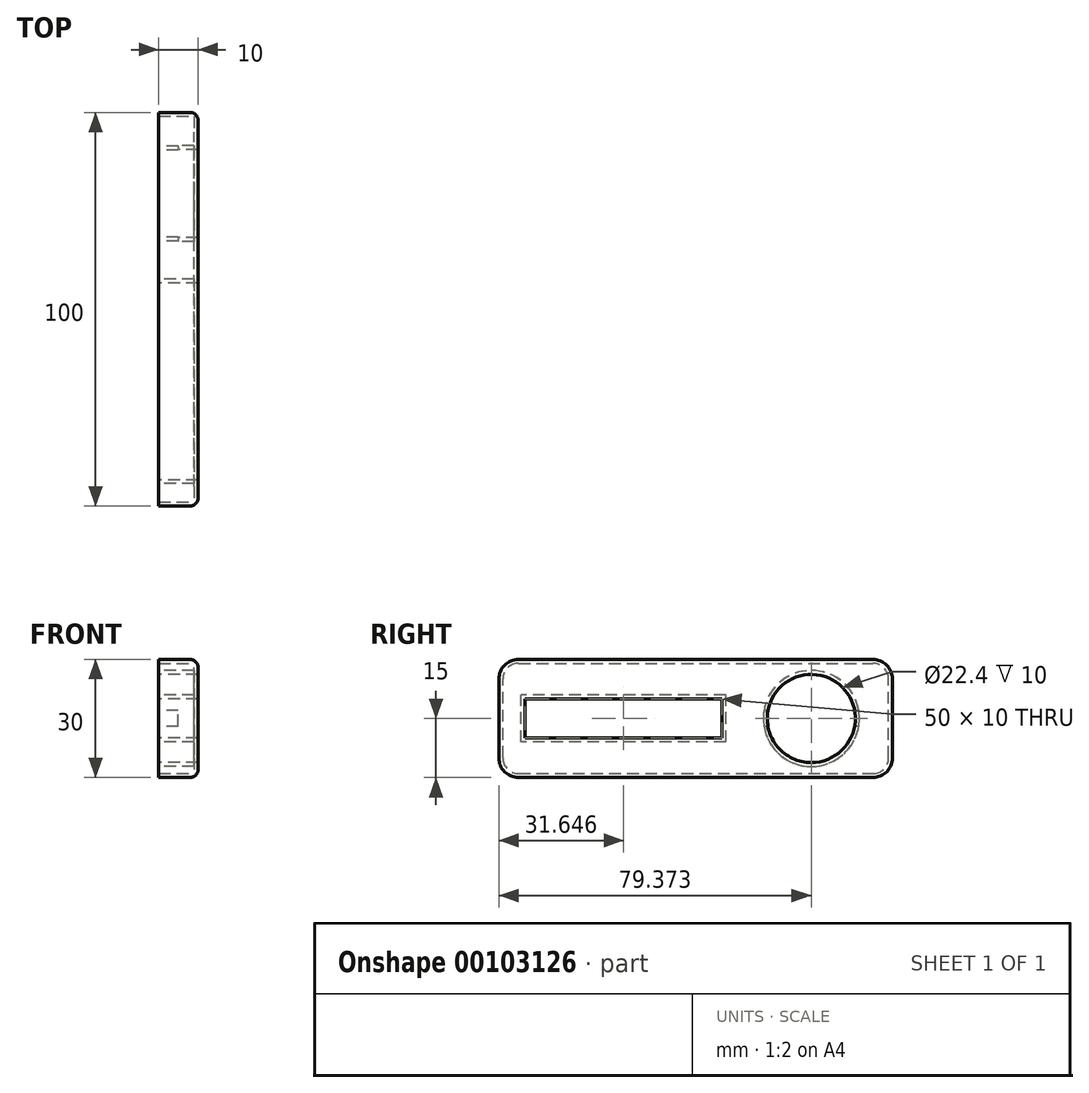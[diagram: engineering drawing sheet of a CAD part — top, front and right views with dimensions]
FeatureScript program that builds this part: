
annotation { "Feature Type Name" : "Feature", "Feature Type Description" : "" }
export const myFeature = defineFeature(function(context is Context, id is Id, definition is map)
    precondition{}
    {
        {
            var Q0;
            Q0=qCreatedBy(makeId("Right.planeOp"),FACE);
            var sketch = newSketch(context, id + "F0", { "sketchPlane" : qUnion([Q0])});
            skLineSegment(sketch, "E0.bottom", {"start": v(-45, -15) * mm, "end": v(45, -15) * mm});
            skLineSegment(sketch, "E0.top", {"start": v(-45, 15) * mm, "end": v(45, 15) * mm});
            skLineSegment(sketch, "E0.left", {"start": v(-50, -10) * mm, "end": v(-50, 10) * mm});
            skLineSegment(sketch, "E0.right", {"start": v(50, -10) * mm, "end": v(50, 10) * mm});
            skPoint(sketch, "E0.middle", {"position": v(0, 0) * mm});
            skPoint(sketch, "E1.visualSharp", {"position": v(50, 15) * mm});
            skArc(sketch, "E1.filletArc", {"start": v(50, 10) * mm, "mid": v(48.54, 13.54) * mm, "end": v(45, 15) * mm});
            skPoint(sketch, "E2.visualSharp", {"position": v(50, -15) * mm});
            skArc(sketch, "E2.filletArc", {"start": v(45, -15) * mm, "mid": v(48.54, -13.54) * mm, "end": v(50, -10) * mm});
            skPoint(sketch, "E3.visualSharp", {"position": v(-50, 15) * mm});
            skArc(sketch, "E3.filletArc", {"start": v(-45, 15) * mm, "mid": v(-48.54, 13.54) * mm, "end": v(-50, 10) * mm});
            skPoint(sketch, "E4.visualSharp", {"position": v(-50, -15) * mm});
            skArc(sketch, "E4.filletArc", {"start": v(-50, -10) * mm, "mid": v(-48.54, -13.54) * mm, "end": v(-45, -15) * mm});
            skLineSegment(sketch, "E5.bottom", {"start": v(6.65, -5) * mm, "end": v(-43.35, -5) * mm});
            skLineSegment(sketch, "E5.top", {"start": v(6.65, 5) * mm, "end": v(-43.35, 5) * mm});
            skLineSegment(sketch, "E5.left", {"start": v(6.65, -5) * mm, "end": v(6.65, 5) * mm});
            skLineSegment(sketch, "E5.right", {"start": v(-43.35, -5) * mm, "end": v(-43.35, 5) * mm});
            skPoint(sketch, "E5.middle", {"position": v(-18.35, 0) * mm});
            skCircle(sketch, "E6", {"center": v(29.37, 0) * mm, "radius": 11.2 * mm});
            skSolve(sketch);
        }
        {
            var Q0;
            Q0=makeQuery(id+"F0.imprint","IMPRINT",FACE,{"disambiguationData":[TD([[makeQuery(id+"F0.imprint","IMPRINT",EDGE,{"derivedFrom":sQuery(id+"F0.wireOp",EDGE,"E0.bottom")}),1.0]])]});
            extrude(context, id + "F1", {"entities" : qUnion([Q0]), "depth" : 10 * mm, "offsetDistance" : 25 * mm});
        }
        {
            var Q0;
            Q0=makeQuery(id+"F1.opExtrude","CAP_FACE",FACE,{"disambiguationData":[OSD([sQuery(id+"F0.wireOp",EDGE,"E0.bottom"),sQuery(id+"F0.wireOp",EDGE,"E0.top"),sQuery(id+"F0.wireOp",EDGE,"E0.left"),sQuery(id+"F0.wireOp",EDGE,"E0.right"),sQuery(id+"F0.wireOp",EDGE,"E1.filletArc"),sQuery(id+"F0.wireOp",EDGE,"E2.filletArc"),sQuery(id+"F0.wireOp",EDGE,"E3.filletArc"),sQuery(id+"F0.wireOp",EDGE,"E4.filletArc"),sQuery(id+"F0.wireOp",EDGE,"E5.bottom"),sQuery(id+"F0.wireOp",EDGE,"E5.top"),sQuery(id+"F0.wireOp",EDGE,"E5.left"),sQuery(id+"F0.wireOp",EDGE,"E5.right"),sQuery(id+"F0.wireOp",EDGE,"E6")])],"isStart":true});
            shell(context, id + "F2", {"entities" : qUnion([Q0]), "thickness" : 1 * mm});
        }
        {
            var Q0;
            Q0=makeQuery(id+"F1.opExtrude","CAP_EDGE",EDGE,{"disambiguationData":[OSD([sQuery(id+"F0.wireOp",EDGE,"E0.bottom")])],"isStart":false});
            fillet(context, id + "F3", {"entities" : qUnion([Q0]), "tangentPropagation" : true, "radius" : 2 * mm, "defaultsChanged" : false, "vertexSettings" : [], "allowEdgeOverflow" : false});
        }
        {
            var Q0;
            {var subQ0=sQuery(id+"F0.wireOp",EDGE,"E6");var subQ1=sQuery(id+"F0.wireOp",EDGE,"E5.right");var subQ2=sQuery(id+"F0.wireOp",EDGE,"E5.left");var subQ3=sQuery(id+"F0.wireOp",EDGE,"E5.top");var subQ4=sQuery(id+"F0.wireOp",EDGE,"E5.bottom");var subQ5=sQuery(id+"F0.wireOp",EDGE,"E4.filletArc");var subQ6=sQuery(id+"F0.wireOp",EDGE,"E3.filletArc");var subQ7=sQuery(id+"F0.wireOp",EDGE,"E2.filletArc");var subQ8=sQuery(id+"F0.wireOp",EDGE,"E1.filletArc");var subQ9=sQuery(id+"F0.wireOp",EDGE,"E0.right");var subQ10=sQuery(id+"F0.wireOp",EDGE,"E0.left");var subQ11=sQuery(id+"F0.wireOp",EDGE,"E0.top");var subQ12=sQuery(id+"F0.wireOp",EDGE,"E0.bottom");Q0=makeQuery(id+"F2.opShell","OFFSET_FACE",FACE,{"disambiguationData":[OSD([subQ12,subQ11,subQ10,subQ9,subQ8,subQ7,subQ6,subQ5,subQ4,subQ3,subQ2,subQ1,subQ0]),TDD([makeQuery(id+"F1.opExtrude","CAP_FACE",FACE,{"disambiguationData":[OSD([subQ12,subQ11,subQ10,subQ9,subQ8,subQ7,subQ6,subQ5,subQ4,subQ3,subQ2,subQ1,subQ0])],"isStart":true})]),OD(1.0)]});}
            var sketch = newSketch(context, id + "F4", { "sketchPlane" : qUnion([Q0])});
            skLineSegment(sketch, "E7.bottom", {"start": v(-43.37, 2) * mm, "end": v(-15.37, 2) * mm});
            skLineSegment(sketch, "E7.top", {"start": v(-43.37, -2) * mm, "end": v(-15.37, -2) * mm});
            skLineSegment(sketch, "E7.left", {"start": v(-43.37, 2) * mm, "end": v(-43.37, -2) * mm});
            skLineSegment(sketch, "E7.right", {"start": v(-15.37, 2) * mm, "end": v(-15.37, -2) * mm});
            skPoint(sketch, "E7.middle", {"position": v(-29.37, 0) * mm});
            skSolve(sketch);
        }
        {
            var Q0;
            {var subQ0=sQuery(id+"F4.wireOp",EDGE,"E7.bottom");var subQ1=makeQuery(id+"F1.opExtrude","CAP_EDGE",EDGE,{"disambiguationData":[OSD([sQuery(id+"F0.wireOp",EDGE,"E6")])],"isStart":true});var subQ2=makeQuery(id+"F4.imprint","INTERSECT",VERTEX,{"disambiguationData":[OD(0.0)],"derivedFrom":[subQ1,subQ0]});Q0=makeQuery(id+"F4.imprint","IMPRINT",FACE,{"disambiguationData":[TD([[makeQuery(id+"F4.imprint","IMPRINT",EDGE,{"disambiguationData":[TD([[subQ2,-1.0]])],"derivedFrom":subQ0}),-1.0]])]});}
            var Q1;
            {var subQ0=sQuery(id+"F4.wireOp",EDGE,"E7.left");Q1=makeQuery(id+"F4.imprint","IMPRINT",FACE,{"disambiguationData":[TD([[makeQuery(id+"F4.imprint","IMPRINT",EDGE,{"derivedFrom":subQ0}),1.0]])]});}
            var Q2;
            {var subQ0=sQuery(id+"F4.wireOp",EDGE,"E7.bottom");var subQ1=sQuery(id+"F0.wireOp",EDGE,"E6");var subQ2=makeQuery(id+"F1.opExtrude","CAP_EDGE",EDGE,{"disambiguationData":[OSD([subQ1])],"isStart":true});var subQ5=makeQuery(id+"F4.imprint","INTERSECT",VERTEX,{"disambiguationData":[OD(1.0)],"derivedFrom":[subQ2,subQ0]});Q2=makeQuery(id+"F4.imprint","IMPRINT",FACE,{"disambiguationData":[TD([[makeQuery(id+"F4.imprint","IMPRINT",EDGE,{"disambiguationData":[TD([[subQ5,-1.0]])],"derivedFrom":subQ2}),1.0]])]});}
            var Q3;
            {var subQ0=sQuery(id+"F4.wireOp",EDGE,"E7.right");Q3=makeQuery(id+"F4.imprint","IMPRINT",FACE,{"disambiguationData":[TD([[makeQuery(id+"F4.imprint","IMPRINT",EDGE,{"derivedFrom":subQ0}),-1.0]])]});}
            var Q4;
            {var subQ0=sQuery(id+"F4.wireOp",EDGE,"E7.bottom");var subQ1=sQuery(id+"F0.wireOp",EDGE,"E6");var subQ2=makeQuery(id+"F1.opExtrude","CAP_EDGE",EDGE,{"disambiguationData":[OSD([subQ1])],"isStart":true});var subQ5=makeQuery(id+"F4.imprint","INTERSECT",VERTEX,{"disambiguationData":[OD(0.0)],"derivedFrom":[subQ2,subQ0]});Q4=makeQuery(id+"F4.imprint","IMPRINT",FACE,{"disambiguationData":[TD([[makeQuery(id+"F4.imprint","IMPRINT",EDGE,{"disambiguationData":[TD([[subQ5,1.0]])],"derivedFrom":subQ2}),1.0]])]});}
            extrude(context, id + "F5", {"entities" : qUnion([Q0, Q1, Q2, Q3, Q4]), "operationType" : NewBodyOperationType.REMOVE, "oppositeDirection" : true, "depth" : 5 * mm, "offsetDistance" : 25 * mm});
        }
    });
